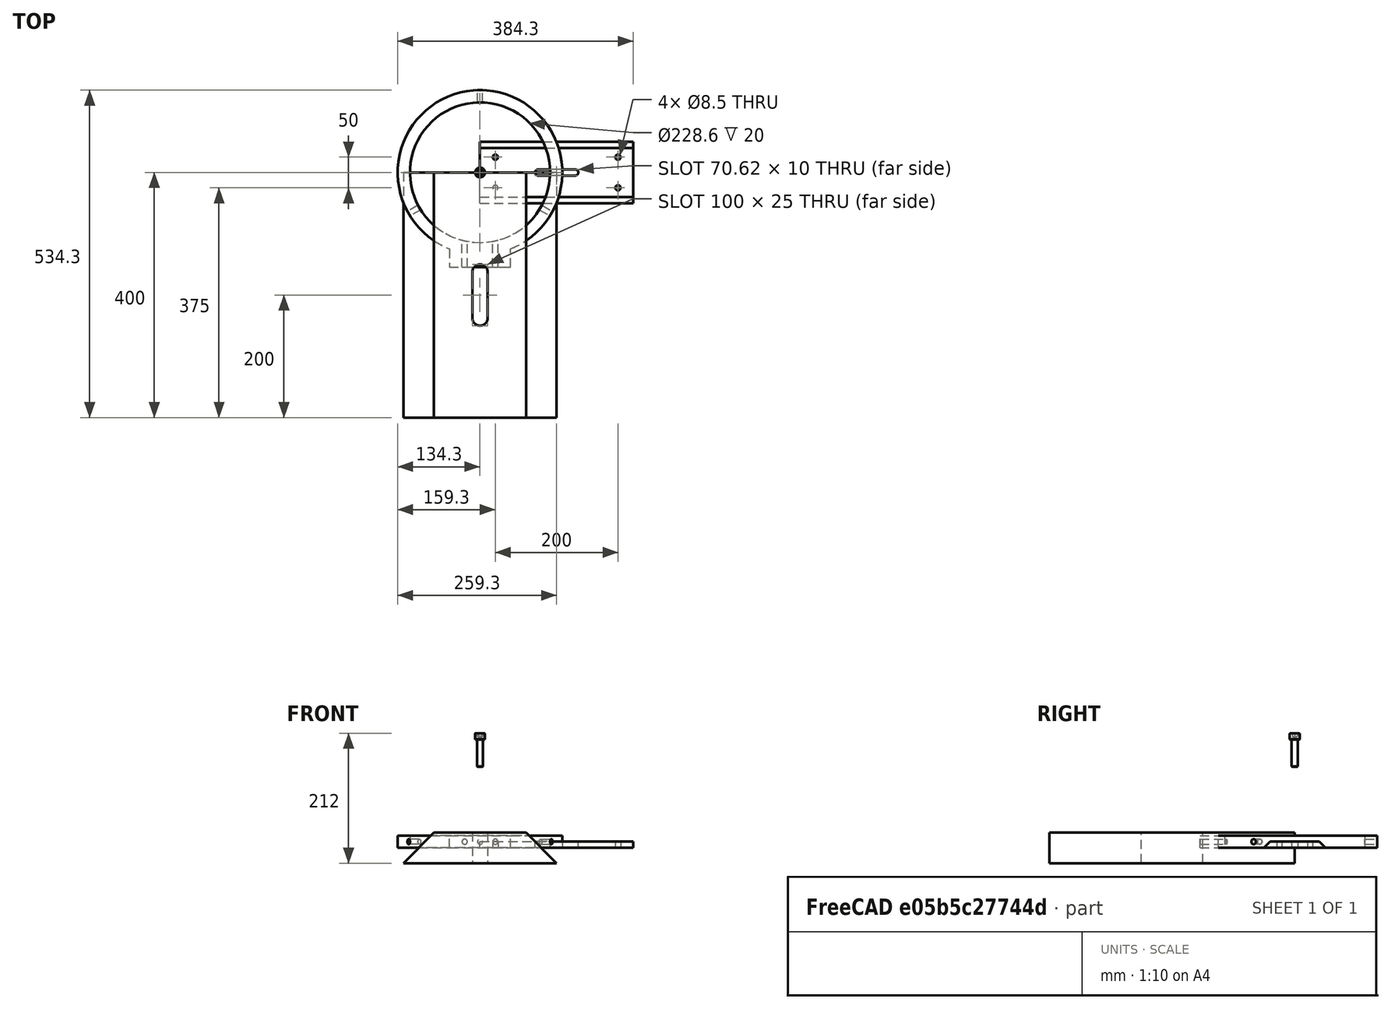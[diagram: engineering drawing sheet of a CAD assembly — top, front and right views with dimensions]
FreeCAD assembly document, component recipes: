
FREECAD ASSEMBLY — COMPONENT RECIPES ("wedge-2")

This assembly document has 5 components, labeled P0..P4 below (a component is one placed body or linked part). 2 of them carry a construction recipe — the FreeCAD feature program that regenerates the part from scratch, quoted from this document or its linked companion documents; the rest are supplied as boundary geometry only. No exploded tour is included for this assembly.
COMPONENT P0 — geometry summary ("M10x45-Screw006"; no construction recipe available for this part):
  bounding box: 55.0 x 16.0 x 16.0 mm
  tessellated surface: 6,916 triangles
  volume: 5174 mm^3 (37% of its bounding box)
  symmetry: revolution-symmetric about the z axis through its bounding-box center
COMPONENT P1 — geometry summary ("M10x45-Screw007"; no construction recipe available for this part):
  bounding box: 55.0 x 16.0 x 16.0 mm
  tessellated surface: 6,916 triangles
  volume: 5174 mm^3 (37% of its bounding box)
  symmetry: revolution-symmetric about the z axis through its bounding-box center
COMPONENT P2 — geometry summary ("M10x45-Screw008"; no construction recipe available for this part):
  bounding box: 53.3 x 37.9 x 16.0 mm
  tessellated surface: 6,916 triangles
  volume: 5174 mm^3 (16% of its bounding box)
COMPONENT P3 — recipe-attached ("Saddle Ring 005", modeled in this document).
Construction recipe (the document's own serialized feature program — sketch geometry with constraints, then the solid features built on it; lengths are millimeters unless a unit is written):

FEATURE [Sketcher::SketchObject] Sketch006
  ArcFitTolerance = 1e-06
  AttachmentSupport = -> [XY_Plane004]
  FullyConstrained = true
  MakeInternals = false
  MapMode = 5
  sketch-geometry (5):
    g0: ArcOfCircle CenterX=0 CenterY=0 CenterZ=0 NormalX=0 NormalY=0 NormalZ=1 AngleXU=0 Radius=134.3 StartAngle=5.09388 EndAngle=10.6141
    g1: Circle CenterX=0 CenterY=0 CenterZ=0 NormalX=0 NormalY=0 NormalZ=1 AngleXU=0 Radius=114.3
    g2: LineSegment StartX=-50 StartY=-124.645 StartZ=0 EndX=-50 EndY=-154.645 EndZ=0
    g3: LineSegment StartX=-50 StartY=-154.645 StartZ=0 EndX=50 EndY=-154.645 EndZ=0
    g4: LineSegment StartX=50 StartY=-154.645 StartZ=0 EndX=50 EndY=-124.645 EndZ=0
  constraints (14):
    c: Coincident(g0,g-1)
    c: Coincident(g1,g0)
    c: Coincident(g2,g3)
    c: Coincident(g3,g4)
    c: Vertical(g2)
    c: Vertical(g4)
    c: Horizontal(g3)
    c: Coincident(g2,g0)
    c: Coincident(g0,g4)
    c: Equal(g4,g2)
    c: Diameter(g1) = 228.6
    c: Distance(g0,g1) = 20
    c: DistanceX(g3,g3) = 100
    c: DistanceY(g2,g2) = 30
FEATURE [PartDesign::Pad] Pad003
  Direction = (0,0,1)
  Length = 20
  Length2 = 10
  Profile = -> Sketch006
  ReferenceAxis = -> Sketch006 [N_Axis]
  Refine = true
  Suppressed = false
  Type = 0
FEATURE [PartDesign::SubShapeBinder] Binder
  BindCopyOnChange = 0
  BindMode = 0
  ClaimChildren = false
  Context = -> Part [Body003.Binder.]
  Fuse = false
  MakeFace = true
  OffsetFill = false
  OffsetIntersection = false
  OffsetJoinType = 0
  OffsetOpenResult = false
  PartialLoad = false
  Placement = pos=(168,0,0) rot=(1,0,0;1.5708rad)
  Refine = true
  Relative = true
  Support = -> [Body002[Sketch004.]]
  _Version = 2
FEATURE [Sketcher::SketchObject] Sketch007
  ArcFitTolerance = 1e-06
  AttachmentSupport = -> [Pad003]
  ExternalGeometry = -> [Binder,Pad003]
  FullyConstrained = false
  MakeInternals = false
  MapMode = 5
  Placement = pos=(0,-154.645,0) rot=(1,0,0;1.5708rad)
  sketch-geometry (5):
    g0: LineSegment [constr] StartX=193 StartY=25 StartZ=0 EndX=193 EndY=-25 EndZ=0
    g1: Circle CenterX=-25 CenterY=10 CenterZ=0 NormalX=0 NormalY=0 NormalZ=1 AngleXU=0 Radius=5.55482
    g2: Circle CenterX=25 CenterY=10 CenterZ=0 NormalX=0 NormalY=0 NormalZ=1 AngleXU=0 Radius=5.55482
    g3: LineSegment [constr] StartX=-25 StartY=10 StartZ=0 EndX=25 EndY=10 EndZ=0
    g4: GeomPoint [constr] X=-5.2e-15 Y=10 Z=0
  constraints (9):
    c: Coincident(g0,g-3)
    c: Coincident(g0,g-4)
    c: Coincident(g3,g2)
    c: Equal(g3,g0)
    c: Symmetric(g1,g2,g-2)
    c: Equal(g2,g1)
    c: Symmetric(g3,g3,g4)
    c: Symmetric(g-6,g-5,g4)
    c: PointOnObject(g1,g3)
FEATURE [PartDesign::Hole] Hole001
  BaseFeature = -> Pad003
  CustomThreadClearance = 0
  Depth = 75
  DepthType = 0
  Diameter = 8.5
  DrillForDepth = false
  DrillPoint = 1
  DrillPointAngle = 118
  HoleCutCountersinkAngle = 90
  HoleCutCustomValues = false
  HoleCutDepth = 0
  HoleCutDiameter = 6.1
  HoleCutType = 0
  ModelThread = false
  Profile = -> Sketch007
  Refine = true
  Suppressed = false
  Tapered = false
  TaperedAngle = 90
  ThreadClass = 0
  ThreadDepth = 75
  ThreadDepthType = 0
  ThreadDirection = 0
  ThreadFit = 0
  ThreadSize = 18
  ThreadType = 1
  Threaded = true
  UseCustomThreadClearance = false
FEATURE [Sketcher::SketchObject] Sketch008
  ArcFitTolerance = 1e-06
  AttachmentSupport = -> [XZ_Plane004]
  ExternalGeometry = -> [Hole001]
  FullyConstrained = true
  MakeInternals = false
  MapMode = 5
  Placement = pos=(0,0,0) rot=(1,0,0;1.5708rad)
  expr: Constraints[0] = 15 mm
  sketch-geometry (2):
    g0: Circle CenterX=0 CenterY=10 CenterZ=0 NormalX=0 NormalY=0 NormalZ=1 AngleXU=0 Radius=7.5
    g1: GeomPoint [constr] X=0 Y=20 Z=0
  constraints (3):
    c: Diameter(g0) = 15
    c: Symmetric(g-3,g-3,g1)
    c: Symmetric(g-1,g1,g0)
FEATURE [PartDesign::Hole] Hole002
  BaseFeature = -> Hole001
  CustomThreadClearance = 0
  Depth = 200
  DepthType = 0
  Diameter = 8.5
  DrillForDepth = false
  DrillPoint = 1
  DrillPointAngle = 118
  HoleCutCountersinkAngle = 90
  HoleCutCustomValues = false
  HoleCutDepth = 0
  HoleCutDiameter = 0
  HoleCutType = 0
  ModelThread = false
  Profile = -> Sketch008
  Refine = true
  Suppressed = false
  Tapered = false
  TaperedAngle = 90
  ThreadClass = 0
  ThreadDepth = 200
  ThreadDepthType = 0
  ThreadDirection = 0
  ThreadFit = 0
  ThreadSize = 18
  ThreadType = 1
  Threaded = true
  UseCustomThreadClearance = false
FEATURE [PartDesign::PolarPattern] PolarPattern001
  Angle = 240
  Axis = -> Sketch008 [V_Axis]
  BaseFeature = -> Hole002
  Mode = 0
  Occurrences = 3
  Offset = 120
  Originals = -> [Hole002]
  Refine = true
  Suppressed = false
  TransformMode = 0
FEATURE [PartDesign::Body] Body003  label="Saddle Ring 2"
  AllowCompound = false
  Group = -> [Sketch006,Pad003,Sketch007,Binder,Hole001,Sketch008,Hole002,PolarPattern001]
  Origin = -> Origin004
  Tip = -> PolarPattern001
COMPONENT P4 — recipe-attached ("Upper Dovetail001", modeled in this document).
Construction recipe (the document's own serialized feature program — sketch geometry with constraints, then the solid features built on it; lengths are millimeters unless a unit is written):

FEATURE [Sketcher::SketchObject] Sketch003
  ArcFitTolerance = 1e-06
  AttachmentSupport = -> [YZ_Plane003]
  FullyConstrained = true
  MakeInternals = false
  MapMode = 5
  Placement = pos=(0,0,0) rot=(0.57735,0.57735,0.57735;2.0944rad)
  sketch-geometry (4):
    g0: LineSegment StartX=-40 StartY=10 StartZ=0 EndX=40 EndY=10 EndZ=0
    g1: LineSegment StartX=-50 StartY=0 StartZ=0 EndX=50 EndY=5e-16 EndZ=0
    g2: LineSegment StartX=-50 StartY=0 StartZ=0 EndX=-40 EndY=10 EndZ=0
    g3: LineSegment StartX=40 StartY=10 StartZ=0 EndX=50 EndY=5e-16 EndZ=0
  constraints (10):
    c: Coincident(g2,g1)
    c: Coincident(g2,g0)
    c: Coincident(g3,g0)
    c: Coincident(g3,g1)
    c: Symmetric(g1,g1,g-2)
    c: Symmetric(g0,g0,g-2)
    c: DistanceX(g1,g1) = 100
    c: Angle(g1,g2) = 0.785398
    c: PointOnObject(g-1,g1)
    c: Distance(g0,g1) = 10
FEATURE [PartDesign::Pad] Pad002
  Direction = (1,0,0)
  Length = 250
  Length2 = 10
  Placement = pos=(0,0,0) rot=(1,1,1;2.0944rad)
  Profile = -> Sketch003
  ReferenceAxis = -> Sketch003 [N_Axis]
  Refine = true
  Suppressed = false
  Type = 0
FEATURE [Sketcher::SketchObject] Sketch004
  ArcFitTolerance = 1e-06
  AttachmentSupport = -> [Pad002]
  ExternalGeometry = -> [Pad002]
  FullyConstrained = false
  MakeInternals = false
  MapMode = 5
  Placement = pos=(0,2.2e-15,10) rot=(0,0,-1;1.5708rad)
  sketch-geometry (10):
    g0: LineSegment [constr] StartX=0 StartY=225 StartZ=0 EndX=1.13e-13 EndY=250 EndZ=0
    g1: LineSegment [constr] StartX=0 StartY=25 StartZ=0 EndX=0 EndY=0 EndZ=0
    g2: LineSegment [constr] StartX=0 StartY=25 StartZ=0 EndX=-25 EndY=25 EndZ=0
    g3: LineSegment [constr] StartX=0 StartY=25 StartZ=0 EndX=25 EndY=25 EndZ=0
    g4: LineSegment [constr] StartX=0 StartY=225 StartZ=0 EndX=-25 EndY=225 EndZ=0
    g5: LineSegment [constr] StartX=0 StartY=225 StartZ=0 EndX=25 EndY=225 EndZ=0
    g6: Circle CenterX=-25 CenterY=25 CenterZ=0 NormalX=0 NormalY=0 NormalZ=1 AngleXU=0 Radius=5.63511
    g7: Circle CenterX=25 CenterY=25 CenterZ=0 NormalX=0 NormalY=0 NormalZ=1 AngleXU=0 Radius=5.63511
    g8: Circle CenterX=25 CenterY=225 CenterZ=0 NormalX=0 NormalY=0 NormalZ=1 AngleXU=0 Radius=5.63511
    g9: Circle CenterX=-25 CenterY=225 CenterZ=0 NormalX=0 NormalY=0 NormalZ=1 AngleXU=0 Radius=5.63511
  constraints (25):
    c: Symmetric(g-3,g-3,g0)
    c: Coincident(g1,g-1)
    c: Equal(g1,g0)
    c: DistanceY(g0,g0) = 25
    c: Coincident(g2,g1)
    c: Horizontal(g2)
    c: Coincident(g3,g1)
    c: Horizontal(g3)
    c: Coincident(g4,g0)
    c: Horizontal(g4)
    c: Coincident(g5,g0)
    c: Horizontal(g5)
    c: Equal(g5,g4)
    c: Equal(g4,g3)
    c: Equal(g3,g2)
    c: PointOnObject(g0,g-2)
    c: Coincident(g6,g2)
    c: Coincident(g7,g3)
    c: Coincident(g8,g5)
    c: Coincident(g9,g4)
    c: Equal(g6,g8)
    c: Equal(g8,g9)
    c: Equal(g9,g7)
    c: DistanceX(g2,g2) = 25
    c: PointOnObject(g1,g-2)
FEATURE [PartDesign::Hole] Hole
  BaseFeature = -> Pad002
  CustomThreadClearance = 0
  Depth = 25
  DepthType = 0
  Diameter = 8.5
  DrillForDepth = false
  DrillPoint = 1
  DrillPointAngle = 118
  HoleCutCountersinkAngle = 90
  HoleCutCustomValues = false
  HoleCutDepth = 0
  HoleCutDiameter = 22.4
  HoleCutType = 0
  ModelThread = false
  Placement = pos=(0,0,0) rot=(1,1,1;2.0944rad)
  Profile = -> Sketch004
  Refine = true
  Suppressed = false
  Tapered = false
  TaperedAngle = 90
  ThreadClass = 0
  ThreadDepth = 25
  ThreadDepthType = 0
  ThreadDirection = 0
  ThreadFit = 0
  ThreadSize = 18
  ThreadType = 1
  Threaded = true
  UseCustomThreadClearance = false
FEATURE [Sketcher::SketchObject] Sketch005
  ArcFitTolerance = 1e-06
  AttachmentSupport = -> [Hole]
  ExternalGeometry = -> [Hole]
  FullyConstrained = false
  MakeInternals = false
  MapMode = 5
  Placement = pos=(0,2.2e-15,10) rot=(0,0,-1;1.5708rad)
  sketch-geometry (6):
    g0: ArcOfCircle CenterX=0 CenterY=155.311 CenterZ=0 NormalX=0 NormalY=0 NormalZ=1 AngleXU=0 Radius=5 StartAngle=2.9e-15 EndAngle=3.14159
    g1: ArcOfCircle CenterX=-3e-16 CenterY=94.6895 CenterZ=0 NormalX=0 NormalY=0 NormalZ=1 AngleXU=0 Radius=5 StartAngle=3.14159 EndAngle=6.28319
    g2: LineSegment StartX=5 StartY=155.311 StartZ=0 EndX=5 EndY=94.6895 EndZ=0
    g3: LineSegment StartX=-5 StartY=155.311 StartZ=0 EndX=-5 EndY=94.6895 EndZ=0
    g4: LineSegment [constr] StartX=0 StartY=0 StartZ=0 EndX=-3e-16 EndY=94.6895 EndZ=0
    g5: LineSegment [constr] StartX=0 StartY=155.311 StartZ=0 EndX=1.781e-13 EndY=250 EndZ=0
  constraints (13):
    c: Tangent(g0,g2) = 1.5708
    c: Tangent(g0,g3) = -1.5708
    c: Tangent(g1,g2) = 1.5708
    c: Tangent(g1,g3) = -1.5708
    c: Equal(g0,g1)
    c: Vertical(g3)
    c: PointOnObject(g0,g-2)
    c: Radius(g0) = 5
    c: Coincident(g4,g-1)
    c: Coincident(g4,g1)
    c: Coincident(g5,g0)
    c: Symmetric(g-3,g-3,g5)
    c: Equal(g5,g4)
FEATURE [PartDesign::Pocket] Pocket002
  BaseFeature = -> Hole
  Direction = (0,0,-1)
  Length = 5
  Length2 = 5
  Placement = pos=(0,0,0) rot=(1,1,1;2.0944rad)
  Profile = -> Sketch005
  ReferenceAxis = -> Sketch005 [N_Axis]
  Refine = true
  Suppressed = false
  Type = 1
FEATURE [PartDesign::Body] Body002  label="Upper Dovetail"
  AllowCompound = false
  Group = -> [Sketch003,Pad002,Sketch004,Hole,Sketch005,Pocket002]
  Origin = -> Origin003
  Tip = -> Pocket002
PROVENANCE & LICENSES
A FreeCAD (.FCStd) document from a public repository crawl; recipes are the document's own serialized feature recipes (and, for linked parts, companion documents' recipes).
License: as declared in the source repository (recorded in the dataset sidecar).
